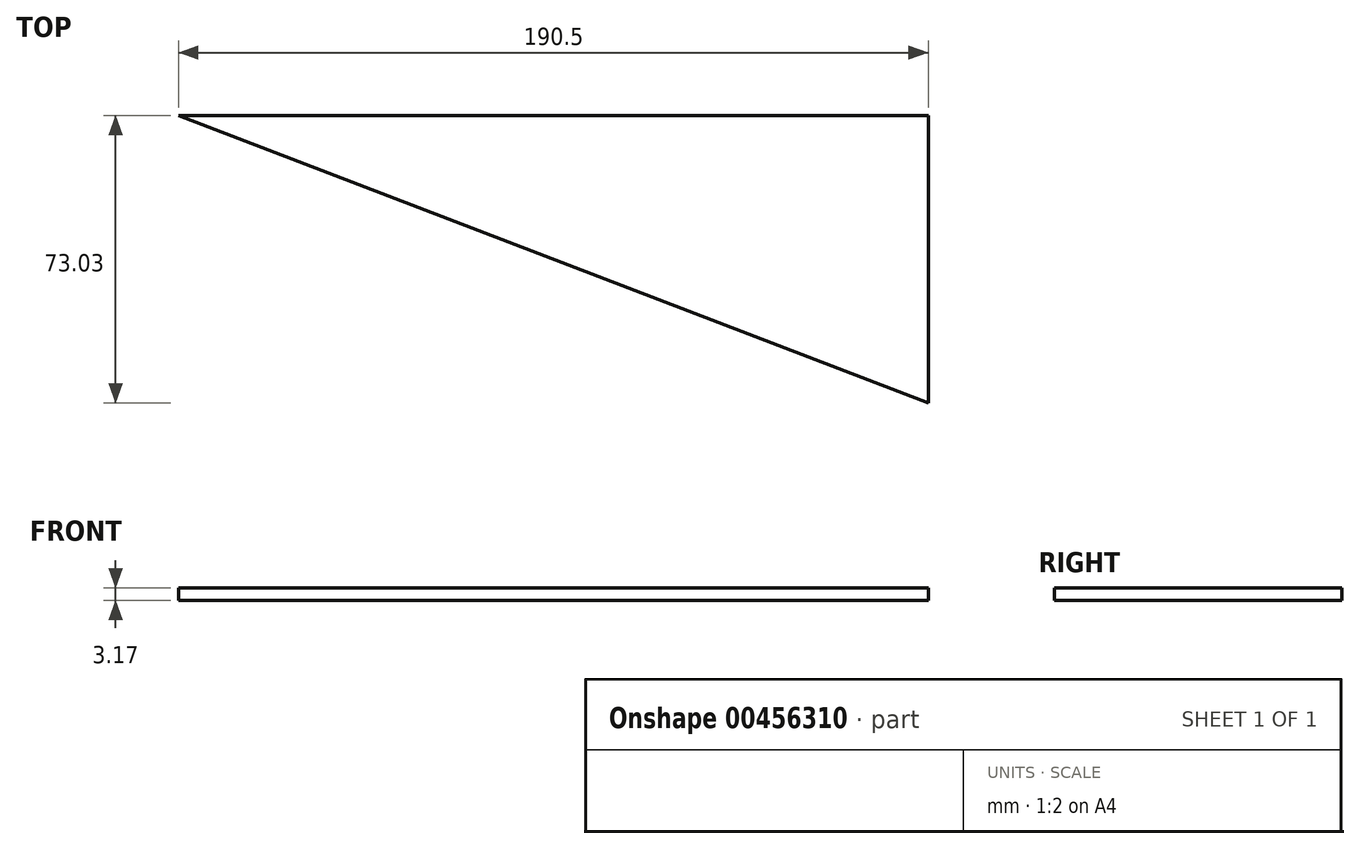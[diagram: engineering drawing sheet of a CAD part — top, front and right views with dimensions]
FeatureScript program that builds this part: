
annotation { "Feature Type Name" : "Feature", "Feature Type Description" : "" }
export const myFeature = defineFeature(function(context is Context, id is Id, definition is map)
    precondition{}
    {
        {
            var Q0;
            Q0=qCreatedBy(makeId("Top.planeOp"),FACE);
            var sketch = newSketch(context, id + "F0", { "sketchPlane" : qUnion([Q0])});
            skLineSegment(sketch, "E0.bottom", {"start": v(0, 0) * mm, "end": v(190.5, 0) * mm});
            skLineSegment(sketch, "E0.top", {"start": v(0, 73.03) * mm, "end": v(190.5, 73.03) * mm});
            skLineSegment(sketch, "E0.left", {"start": v(0, 0) * mm, "end": v(0, 73.02) * mm});
            skLineSegment(sketch, "E0.right", {"start": v(190.5, 0) * mm, "end": v(190.5, 73.03) * mm});
            skSolve(sketch);
        }
        {
            var Q0;
            Q0=makeQuery(id+"F0.imprint","IMPRINT",FACE,{"disambiguationData":[TD([[makeQuery(id+"F0.imprint","IMPRINT",EDGE,{"derivedFrom":sQuery(id+"F0.wireOp",EDGE,"E0.bottom")}),1.0]])]});
            extrude(context, id + "F1", {"entities" : qUnion([Q0]), "depth" : 3.17 * mm});
        }
        {
            var Q0;
            Q0=makeQuery(id+"F1.opExtrude","CAP_FACE",FACE,{"disambiguationData":[OSD([sQuery(id+"F0.wireOp",EDGE,"E0.bottom"),sQuery(id+"F0.wireOp",EDGE,"E0.top"),sQuery(id+"F0.wireOp",EDGE,"E0.left"),sQuery(id+"F0.wireOp",EDGE,"E0.right")])],"isStart":false});
            var sketch = newSketch(context, id + "F2", { "sketchPlane" : qUnion([Q0])});
            skLineSegment(sketch, "E1", {"start": v(0, 73.02) * mm, "end": v(190.5, 0) * mm});
            skSolve(sketch);
        }
        {
            var Q0;
            Q0=makeQuery(id+"F2.imprint","IMPRINT",FACE,{"disambiguationData":[TD([[makeQuery(id+"F2.imprint","IMPRINT",EDGE,{"derivedFrom":sQuery(id+"F2.wireOp",EDGE,"E1")}),-1.0]])]});
            extrude(context, id + "F3", {"entities" : qUnion([Q0]), "operationType" : NewBodyOperationType.REMOVE, "oppositeDirection" : true, "depth" : 25.4 * mm});
        }
    });
